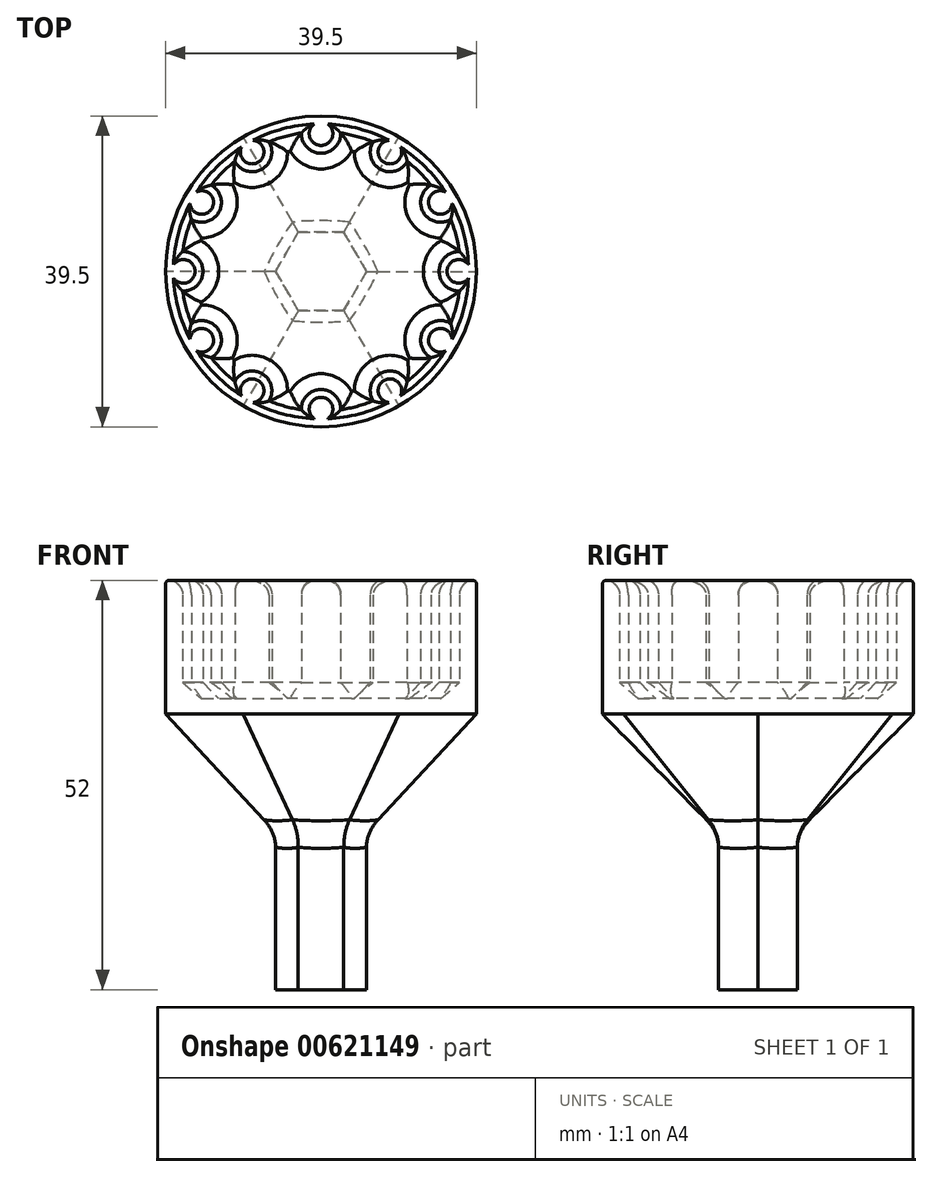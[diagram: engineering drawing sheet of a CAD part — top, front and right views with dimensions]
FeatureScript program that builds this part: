
annotation { "Feature Type Name" : "Feature", "Feature Type Description" : "" }
export const myFeature = defineFeature(function(context is Context, id is Id, definition is map)
    precondition{}
    {
        {
            var Q0;
            Q0=qCreatedBy(makeId("Top.planeOp"),FACE);
            var sketch = newSketch(context, id + "F0", { "sketchPlane" : qUnion([Q0])});
            skCircle(sketch, "E0", {"center": v(0, 0) * mm, "radius": 17.75 * mm});
            skCircle(sketch, "E1", {"center": v(0, 0) * mm, "radius": 15 * mm, "construction": true});
            skArc(sketch, "E2", {"start": v(-2.5, 17.57) * mm, "mid": v(0, 15) * mm, "end": v(2.5, 17.57) * mm});
            skLineSegment(sketch, "E3", {"start": v(0, 0) * mm, "end": v(0, 17.5) * mm, "construction": true});
            skCircle(sketch, "E4", {"center": v(0, 0) * mm, "radius": 19.75 * mm});
            skSolve(sketch);
        }
        {
            var Q0;
            Q0=makeQuery(id+"F0.imprint","IMPRINT",FACE,{"disambiguationData":[TD([[makeQuery(id+"F0.imprint","IMPRINT",EDGE,{"derivedFrom":sQuery(id+"F0.wireOp",EDGE,"E4")}),1.0]])]});
            var Q1;
            {var subQ0=sQuery(id+"F0.wireOp",EDGE,"E2");Q1=makeQuery(id+"F0.imprint","IMPRINT",FACE,{"disambiguationData":[TD([[makeQuery(id+"F0.imprint","IMPRINT",EDGE,{"derivedFrom":subQ0}),1.0]])]});}
            extrude(context, id + "F1", {"entities" : qUnion([Q0, Q1]), "depth" : 15 * mm, "offsetDistance" : 25 * mm});
        }
        {
            var Q0;
            Q0=makeQuery(id+"F1.opExtrude","CAP_EDGE",EDGE,{"disambiguationData":[OSD([sQuery(id+"F0.wireOp",EDGE,"E2")])],"isStart":false});
            var Q1;
            Q1=makeQuery(id+"F1.opExtrude","CAP_EDGE",EDGE,{"disambiguationData":[OSD([sQuery(id+"F0.wireOp",EDGE,"E0")])],"isStart":false});
            chamfer(context, id + "F2", {"entities" : qUnion([Q0, Q1]), "width" : 1 * mm, "tangentPropagation" : true});
        }
        {
            var Q0;
            {var subQ0=sQuery(id+"F0.wireOp",EDGE,"E2");Q0=makeQuery(id+"F2.opChamfer","BLEND_EDGE",EDGE,{"blendedFrom":[makeQuery(id+"F1.opExtrude","CAP_EDGE",EDGE,{"disambiguationData":[OSD([subQ0])],"isStart":false}),makeQuery(id+"F1.opExtrude","SWEPT_FACE",FACE,{"disambiguationData":[OSD([subQ0])]})],"blendedInto":[makeQuery(id+"F1.opExtrude","SWEPT_FACE",FACE,{"disambiguationData":[OSD([subQ0])]})]});}
            var Q1;
            {var subQ0=sQuery(id+"F0.wireOp",EDGE,"E0");Q1=makeQuery(id+"F2.opChamfer","BLEND_EDGE",EDGE,{"blendedFrom":[makeQuery(id+"F1.opExtrude","CAP_EDGE",EDGE,{"disambiguationData":[OSD([subQ0])],"isStart":false}),makeQuery(id+"F1.opExtrude","SWEPT_FACE",FACE,{"disambiguationData":[OSD([subQ0])]})],"blendedInto":[makeQuery(id+"F1.opExtrude","SWEPT_FACE",FACE,{"disambiguationData":[OSD([subQ0])]})]});}
            fillet(context, id + "F3", {"entities" : qUnion([Q0, Q1]), "radius" : 2 * mm, "tangentPropagation" : true, "allowEdgeOverflow" : false});
        }
        {
            var Q0;
            Q0=makeQuery(id+"F1.opExtrude","CAP_EDGE",EDGE,{"disambiguationData":[OSD([sQuery(id+"F0.wireOp",EDGE,"E4")])],"isStart":false});
            fillet(context, id + "F4", {"entities" : qUnion([Q0]), "radius" : .5 * mm, "tangentPropagation" : true, "allowEdgeOverflow" : false});
        }
        {
            var Q0;
            Q0=makeQuery(id+"F1.opExtrude","SWEPT_BODY",BODY,{"disambiguationData":[OSD([sQuery(id+"F0.wireOp",EDGE,"E0"),sQuery(id+"F0.wireOp",EDGE,"E2"),sQuery(id+"F0.wireOp",EDGE,"E4")])]});
            var Q1;
            Q1=makeQuery(id+"F1.opExtrude","SWEPT_FACE",FACE,{"disambiguationData":[OSD([sQuery(id+"F0.wireOp",EDGE,"E4")])]});
            circularPattern(context, id + "F5", {"operationType" : NewBodyOperationType.ADD, "entities" : qUnion([Q0]), "axis" : qUnion([Q1]), "angle" : 360 * degree, "instanceCount" : 12, "equalSpace" : true});
        }
        {
            var Q0;
            {var subQ0=sQuery(id+"F0.wireOp",EDGE,"E2");Q0=makeQuery(id+"F0.imprint","IMPRINT",FACE,{"disambiguationData":[TD([[makeQuery(id+"F0.imprint","IMPRINT",EDGE,{"derivedFrom":subQ0}),-1.0]])]});}
            var Q1;
            {var subQ0=sQuery(id+"F0.wireOp",EDGE,"E2");Q1=makeQuery(id+"F0.imprint","IMPRINT",FACE,{"disambiguationData":[TD([[makeQuery(id+"F0.imprint","IMPRINT",EDGE,{"derivedFrom":subQ0}),1.0]])]});}
            var Q2;
            Q2=makeQuery(id+"F0.imprint","IMPRINT",FACE,{"disambiguationData":[TD([[makeQuery(id+"F0.imprint","IMPRINT",EDGE,{"derivedFrom":sQuery(id+"F0.wireOp",EDGE,"E4")}),1.0]])]});
            extrude(context, id + "F6", {"entities" : qUnion([Q0, Q1, Q2]), "operationType" : NewBodyOperationType.ADD, "oppositeDirection" : true, "depth" : 2 * mm, "offsetDistance" : 25 * mm});
        }
        {
            var Q0;
            Q0=makeQuery(id+"F6.opExtrude","CAP_FACE",FACE,{"disambiguationData":[OSD([sQuery(id+"F0.wireOp",EDGE,"E4")])],"isStart":true});
            chamfer(context, id + "F7", {"entities" : qUnion([Q0]), "width" : 2 * mm, "tangentPropagation" : true});
        }
        {
            var Q0;
            Q0=makeQuery(id+"F6.opExtrude","CAP_FACE",FACE,{"disambiguationData":[OSD([sQuery(id+"F0.wireOp",EDGE,"E4")])],"isStart":false});
            cPlane(context, id + "F8", {"entities" : qUnion([Q0]), "cplaneType" : CPlaneType.OFFSET, "offset" : 15 * mm, "width" : 150 * mm, "height" : 150 * mm});
        }
        {
            var Q0;
            Q0=qCreatedBy(id+"F8.planeOp",FACE);
            var sketch = newSketch(context, id + "F9", { "sketchPlane" : qUnion([Q0])});
            skCircle(sketch, "E5.cCircle", {"center": v(0, 0) * mm, "radius": 5 * mm, "construction": true});
            skLineSegment(sketch, "E5.0", {"start": v(5.77, 0) * mm, "end": v(2.89, -5) * mm});
            skLineSegment(sketch, "E5.1", {"start": v(2.89, -5) * mm, "end": v(-2.89, -5) * mm});
            skLineSegment(sketch, "E5.2", {"start": v(-2.89, -5) * mm, "end": v(-5.77, 0) * mm});
            skLineSegment(sketch, "E5.3", {"start": v(-5.77, 0) * mm, "end": v(-2.89, 5) * mm});
            skLineSegment(sketch, "E5.4", {"start": v(-2.89, 5) * mm, "end": v(2.89, 5) * mm});
            skLineSegment(sketch, "E5.5", {"start": v(2.89, 5) * mm, "end": v(5.77, 0) * mm});
            skPoint(sketch, "E5.0.midPoint", {"position": v(4.33, -2.5) * mm});
            skSolve(sketch);
        }
        {
            var Q0;
            Q0=makeQuery(id+"F9.imprint","IMPRINT",FACE,{"disambiguationData":[TD([[makeQuery(id+"F9.imprint","IMPRINT",EDGE,{"derivedFrom":sQuery(id+"F9.wireOp",EDGE,"E5.0")}),-1.0]])]});
            extrude(context, id + "F10", {"entities" : qUnion([Q0]), "depth" : 20 * mm, "offsetDistance" : 25 * mm});
        }
        {
            var Q1;
            Q1=makeQuery(id+"F10.opExtrude","CAP_FACE",FACE,{"disambiguationData":[OSD([sQuery(id+"F9.wireOp",EDGE,"E5.0"),sQuery(id+"F9.wireOp",EDGE,"E5.1"),sQuery(id+"F9.wireOp",EDGE,"E5.2"),sQuery(id+"F9.wireOp",EDGE,"E5.3"),sQuery(id+"F9.wireOp",EDGE,"E5.4"),sQuery(id+"F9.wireOp",EDGE,"E5.5")])],"isStart":true});
            var Q2;
            Q2=makeQuery(id+"F6.opExtrude","CAP_FACE",FACE,{"disambiguationData":[OSD([sQuery(id+"F0.wireOp",EDGE,"E4")])],"isStart":false});
            loft(context, id + "F11", {"operationType" : NewBodyOperationType.ADD, "sheetProfilesArray" : [{ "sheetProfileEntities" : qUnion([Q1]) }, { "sheetProfileEntities" : qUnion([Q2]) }]});
        }
        {
            var Q0;
            {var subQ0=sQuery(id+"F9.wireOp",EDGE,"E5.1");Q0=makeQuery(id+"F11.boolean.opBoolean","MERGE",EDGE,{"derivedFrom":[makeQuery(id+"F10.opExtrude","CAP_EDGE",EDGE,{"disambiguationData":[OSD([subQ0])],"isStart":true}),makeQuery(id+"F11.opLoft","MID_CAP_EDGE",EDGE,{"disambiguationData":[OSD([sQuery(id+"F9.wireOp",EDGE,"E5.0"),subQ0,sQuery(id+"F9.wireOp",EDGE,"E5.2")])],"capPos":0.0})]});}
            var Q1;
            {var subQ0=sQuery(id+"F9.wireOp",EDGE,"E5.2");Q1=makeQuery(id+"F11.boolean.opBoolean","MERGE",EDGE,{"derivedFrom":[makeQuery(id+"F10.opExtrude","CAP_EDGE",EDGE,{"disambiguationData":[OSD([subQ0])],"isStart":true}),makeQuery(id+"F11.opLoft","MID_CAP_EDGE",EDGE,{"disambiguationData":[OSD([sQuery(id+"F9.wireOp",EDGE,"E5.1"),subQ0,sQuery(id+"F9.wireOp",EDGE,"E5.3")])],"capPos":0.0})]});}
            var Q2;
            {var subQ0=sQuery(id+"F9.wireOp",EDGE,"E5.3");Q2=makeQuery(id+"F11.boolean.opBoolean","MERGE",EDGE,{"derivedFrom":[makeQuery(id+"F10.opExtrude","CAP_EDGE",EDGE,{"disambiguationData":[OSD([subQ0])],"isStart":true}),makeQuery(id+"F11.opLoft","MID_CAP_EDGE",EDGE,{"disambiguationData":[OSD([sQuery(id+"F9.wireOp",EDGE,"E5.2"),subQ0,sQuery(id+"F9.wireOp",EDGE,"E5.4")])],"capPos":0.0})]});}
            var Q3;
            {var subQ0=sQuery(id+"F9.wireOp",EDGE,"E5.4");Q3=makeQuery(id+"F11.boolean.opBoolean","MERGE",EDGE,{"derivedFrom":[makeQuery(id+"F10.opExtrude","CAP_EDGE",EDGE,{"disambiguationData":[OSD([subQ0])],"isStart":true}),makeQuery(id+"F11.opLoft","MID_CAP_EDGE",EDGE,{"disambiguationData":[OSD([sQuery(id+"F9.wireOp",EDGE,"E5.3"),subQ0,sQuery(id+"F9.wireOp",EDGE,"E5.5")])],"capPos":0.0})]});}
            var Q4;
            {var subQ0=sQuery(id+"F9.wireOp",EDGE,"E5.5");Q4=makeQuery(id+"F11.boolean.opBoolean","MERGE",EDGE,{"derivedFrom":[makeQuery(id+"F10.opExtrude","CAP_EDGE",EDGE,{"disambiguationData":[OSD([subQ0])],"isStart":true}),makeQuery(id+"F11.opLoft","MID_CAP_EDGE",EDGE,{"disambiguationData":[OSD([sQuery(id+"F9.wireOp",EDGE,"E5.0"),sQuery(id+"F9.wireOp",EDGE,"E5.4"),subQ0])],"capPos":0.0})]});}
            var Q5;
            {var subQ0=sQuery(id+"F9.wireOp",EDGE,"E5.0");Q5=makeQuery(id+"F11.boolean.opBoolean","MERGE",EDGE,{"derivedFrom":[makeQuery(id+"F10.opExtrude","CAP_EDGE",EDGE,{"disambiguationData":[OSD([subQ0])],"isStart":true}),makeQuery(id+"F11.opLoft","MID_CAP_EDGE",EDGE,{"disambiguationData":[OSD([subQ0,sQuery(id+"F9.wireOp",EDGE,"E5.1"),sQuery(id+"F9.wireOp",EDGE,"E5.5")])],"capPos":0.0})]});}
            fillet(context, id + "F12", {"entities" : qUnion([Q0, Q1, Q2, Q3, Q4, Q5]), "radius" : 5 * mm, "tangentPropagation" : true, "allowEdgeOverflow" : false});
        }
    });
